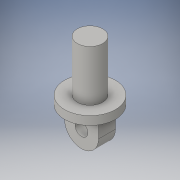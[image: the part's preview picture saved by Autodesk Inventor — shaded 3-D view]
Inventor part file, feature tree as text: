
AUTODESK INVENTOR PART (.ipt)
format: ipt  version: 2016 (Build 200138000, 138)  size: 126,976 bytes
history: native  units: in
note: dims shown in document units (in); Inventor stores cm internally (conversion verified against a paired STEP export)
features: sketch x3, extrude x2, revolve x1, fillet x1, projected_geometry x1
ambient origin geometry x8: Origin, YZ Plane, XZ Plane, XY Plane, X Axis, Y Axis, Z Axis, Center Point
bodies: Solid1 (feature_tree)
feature tree (8):
  revolve  "Revolution1"  [1 undecoded]
  extrude  "Extrusion3"  Depth=2.0in TaperAngle=0.0deg
  fillet  "Fillet2"  Radius=1.0in
  extrude  "Extrusion4"  Depth=2.0in TaperAngle=0.0deg
  sketch  "Sketch1"  dims[d4=90.0deg d5=2.0in]
  sketch  "Sketch2"  dims[d6=2.0in d13=2.0in d14=0.0in d15=1.0in]
  sketch  "Sketch4"  dims[d16=0.75in d17=2.0in d18=0.0in]
  projected_geometry  "Projected Loop2"
note: 1 required parameter value undecoded (feature->parameter linkage not recoverable at this tier; creation-order binding heuristic only, values carry confidence <= 0.55)
